# Revit family: LeL Metope 2.1
name_source: partatom
category: Lighting Fixtures
units: mm (PartAtom-declared; Revit-internal decimal feet)

## family parameters
Cut with Voids When Loaded = Yes
Host = Face
Light Source = No
Part Type = Normal
Room Calculation Point = No
Round Connector Dimension = Use Diameter
Shared = No

## types (10) — shared parameters
CCT = 3000 K
CRI = 80
Default Elevation = 1219 mm
Description = Outdoor Wall Mounted
Height = 60 mm  [stored 0.19685 ft]
IK = IK05
IP = IP65
Lamp = LED
Lenght = 35 mm  [stored 0.114829 ft]
Manufacturer = L&L Luce&Light
Model = TM21
URL = https://www.lucelight.it
Weight = 0.60 kg
Widht = 15 mm  [stored 0.0492126 ft]

## per-type parameters (varying)
| type | Alimentazione | Apparent Load | Lumen Output | Photometry2 | Rated Power supply | Wattage |
| 2.1 D 7W 24Vdc | 24 V | 7 VA | 460 lm | TM2 Light source : 2.1 D 7W 24Vdc | 24 V | 7 W |
| 2.1 D 9W 110-230Vac | 230 V | 9 VA | 460 lm | TM2 Light source : 2.1 D 9W 110-230Vac | 230 V | 9 W |
| 2.1 K 52° 7W 24Vdc | 24 V | 7 VA | 501 lm | TM2 Light source : 2.1 K 52° 7W 24Vdc | 24 V | 7 W |
| 2.1 K 52° 9W 110-230Vac | 230 V | 9 VA | 501 lm | TM2 Light source : 2.1 K 52° 9W 110-230Vac | 230 V | 9 W |
| 2.1 L 36° 7W 24Vdc | 24 V | 7 VA | 430 lm | TM2 Light source : 2.1 L 36° 7W 24Vdc | 24 V | 7 W |
| 2.1 L 36° 9W 110-230Vac | 230 V | 9 VA | 430 lm | TM2 Light source : 2.1 L 36° 9W 110-230Vac | 230 V | 9 W |
| 2.1 M 26° 7W 24Vdc | 24 V | 7 VA | 468 lm | TM2 Light source : 2.1 M 26° 7W 24Vdc | 24 V | 7 W |
| 2.1 M 26° 9W 110-230Vac | 230 V | 9 VA | 468 lm | TM2 Light source : 2.1 M 26° 9W 110-230Vac | 230 V | 9 W |
| 2.1 S 21° 7W 24Vdc | 24 V | 7 VA | 466 lm | TM2 Light source : 2.1 S 21° 7W 24Vdc | 24 V | 7 W |
| 2.1 S 21° 9W 110-230Vac | 230 V | 9 VA | 466 lm | TM2 Light source : 2.1 S 21° 9W 110-230Vac | 230 V | 9 W |

note: [stored X ft] marks values corroborated as IEEE doubles in the binary element streams (Revit-internal decimal feet)
